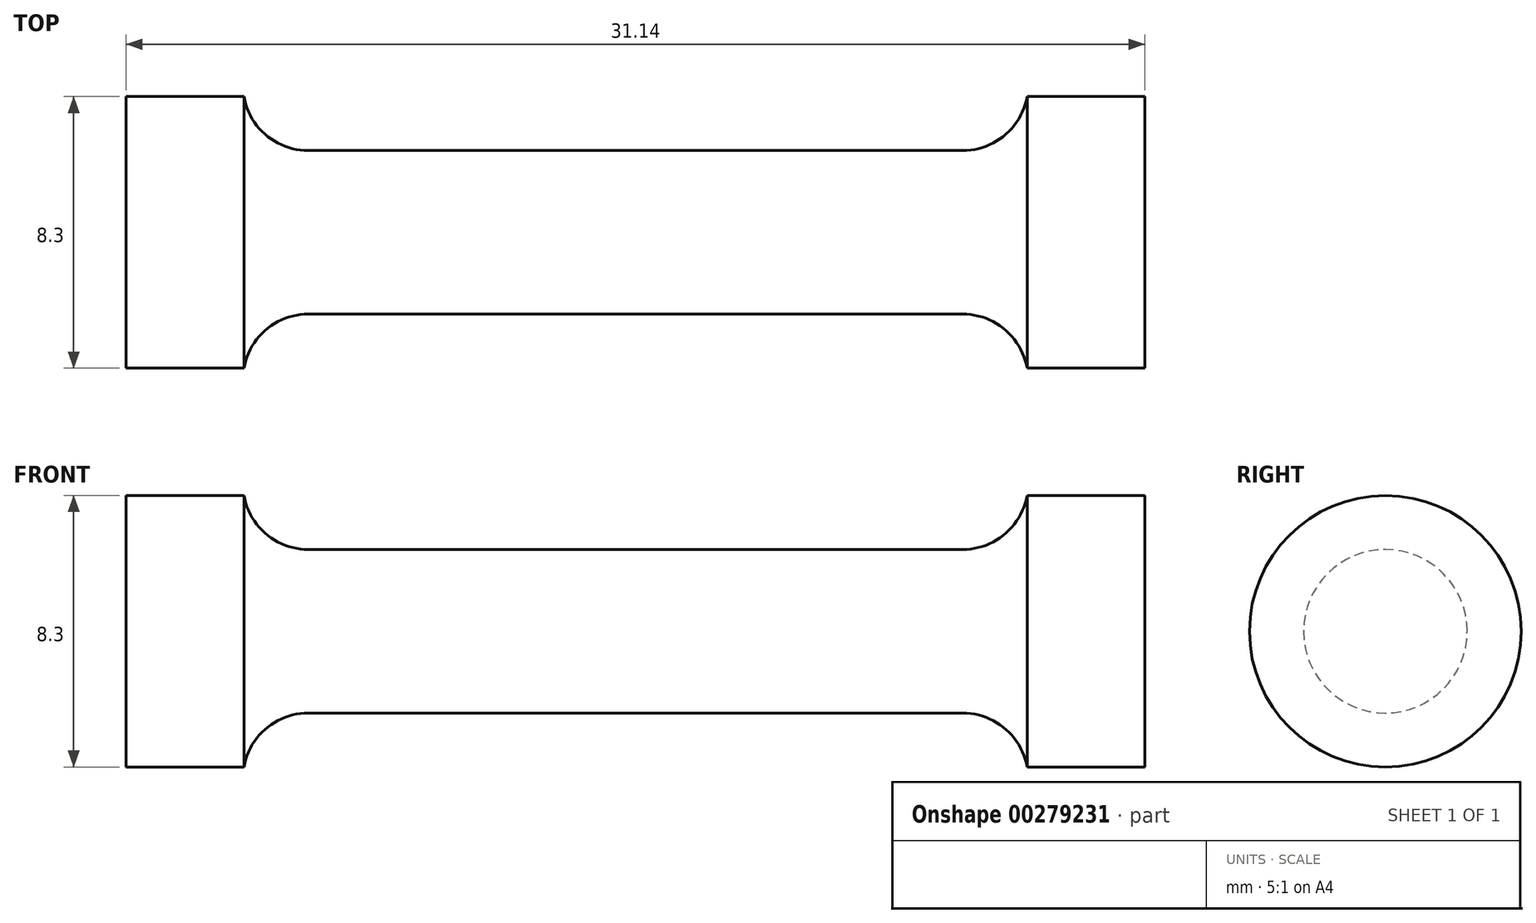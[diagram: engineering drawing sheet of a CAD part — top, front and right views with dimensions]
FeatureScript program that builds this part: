
annotation { "Feature Type Name" : "Feature", "Feature Type Description" : "" }
export const myFeature = defineFeature(function(context is Context, id is Id, definition is map)
    precondition{}
    {
        {
            var Q0;
            Q0=qCreatedBy(makeId("Front.planeOp"),FACE);
            var sketch = newSketch(context, id + "F0", { "sketchPlane" : qUnion([Q0])});
            skLineSegment(sketch, "E0", {"start": v(0, 2.5) * mm, "end": v(10, 2.5) * mm});
            skArc(sketch, "E1", {"start": v(10, 2.5) * mm, "mid": v(11.29, 2.97) * mm, "end": v(11.97, 4.15) * mm});
            skLineSegment(sketch, "E2", {"start": v(11.97, 4.15) * mm, "end": v(15.57, 4.15) * mm});
            skLineSegment(sketch, "E3", {"start": v(15.57, 4.15) * mm, "end": v(15.57, 0) * mm});
            skLineSegment(sketch, "E4.MirrorCS", {"start": v(-15.57, 4.15) * mm, "end": v(-15.57, 0) * mm});
            skArc(sketch, "E5.MirrorCS", {"start": v(-10, 2.5) * mm, "mid": v(-11.29, 2.97) * mm, "end": v(-11.97, 4.15) * mm});
            skLineSegment(sketch, "E6.MirrorCS", {"start": v(0, 2.5) * mm, "end": v(-10, 2.5) * mm});
            skLineSegment(sketch, "E7.MirrorCS", {"start": v(-11.97, 4.15) * mm, "end": v(-15.57, 4.15) * mm});
            skLineSegment(sketch, "E8", {"start": v(-15.57, 0) * mm, "end": v(15.57, 0) * mm});
            skSolve(sketch);
        }
        {
            var Q0;
            Q0 = qSketchRegion(id + "F0", true);
            var Q1;
            Q1=sQuery(id+"F0.wireOp",EDGE,"E8");
            revolve(context, id + "F1", {"entities" : qUnion([Q0]), "axis" : qUnion([Q1]), "revolveType" : RevolveType.FULL});
        }
    });
